# Revit family: MAKROS Panel aislante de entrepiso
name_source: partatom
category: Structural Framing
revit_build: Autodesk Revit 2016 (Build: 20150220_1215(x64)
units: mm (PartAtom-declared; Revit-internal decimal feet)

## family parameters
Always export as geometry = No
Always vertical = Yes
Cut with Voids When Loaded = No
Display in Hidden Views = Edges Hidden by Other Members
Material for Model Behavior = Precast Concrete
OmniClass Number = 23.25.30.11.14.14
OmniClass Title = Beams
Section Shape = Not Defined
Shared = No
Show family pre-cut in plan views = Yes

## types (5) — shared parameters
Adsorción de humedad (Peso) = 1.03%
Adsorción de humedad (Volumen) = 0.020 %
Aislamiento acústico (STC) = 47 dB
Ancho = 60 cm
Conductividad Termica = 0.0344 W/m•K
Densidad Aparente = 19.05 kg/m³
Manufacturer = NOVIDESA
Model = MAKROS
Permeabilidad de vapor de agua = 0.049 ng/Pa•s•m
URL = www.novidesa.com.mx

## per-type parameters (varying)
| type | Espesor | Peso de EPS + canaleta kg/ml | Peso de EPS kg/ml |
| 18 | 18 cm | 3.42 | 1.62 |
| 20 | 20 cm | 3.67 | 1.87 |
| 25 | 25 cm | 4.16 | 2.39 |
| 29 | 29 cm | 4.55 | 2.75 |
| 32 | 32 cm | 4.66 | 2.86 |

## geometry (parser evidence)
native form markers: Blend x2, Sweep x3
no freeform markers — native parametric forms only
